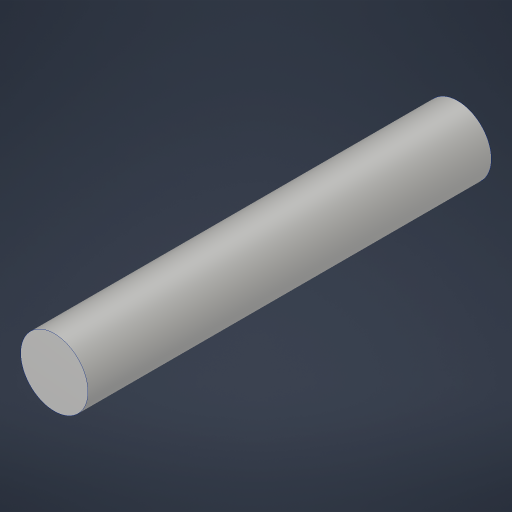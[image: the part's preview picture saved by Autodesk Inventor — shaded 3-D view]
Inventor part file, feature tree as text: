
AUTODESK INVENTOR PART (.ipt)
format: ipt  version: 2023.4 (Build 274418000, 418)  size: 161,280 bytes
history: native  units: in
note: dims shown in document units (in); Inventor stores cm internally (conversion verified against a paired STEP export)
features: extrude x1, sketch x1
ambient origin geometry x8: Origin, YZ Plane, XZ Plane, XY Plane, X Axis, Y Axis, Z Axis, Center Point
bodies: Solid1 (feature_tree)
feature tree (2):
  extrude  "Extrusion1"  Depth=3.0in TaperAngle=0.0deg
  sketch  "Sketch1"  dims[d0=0.5in d1=3.0in d2=0.0in]
